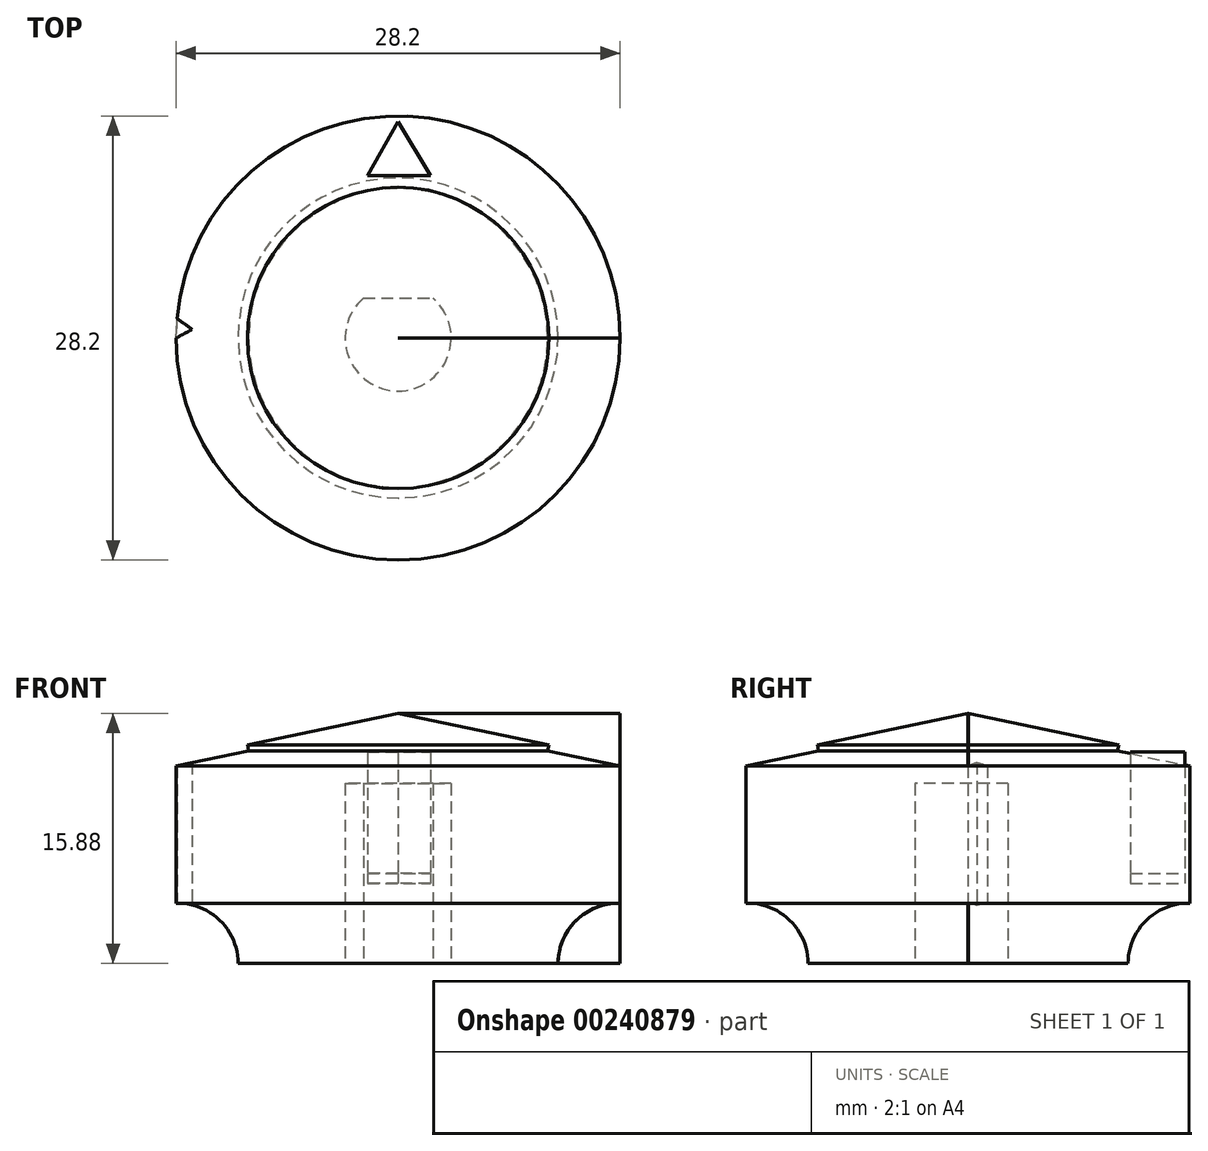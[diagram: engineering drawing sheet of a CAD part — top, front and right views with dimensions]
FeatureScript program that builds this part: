
annotation { "Feature Type Name" : "Feature", "Feature Type Description" : "" }
export const myFeature = defineFeature(function(context is Context, id is Id, definition is map)
    precondition{}
    {
        {
            var Q0;
            Q0=qCreatedBy(makeId("Top.planeOp"),FACE);
            cPlane(context, id + "F0", {"entities" : qUnion([Q0]), "cplaneType" : CPlaneType.OFFSET, "offset" : 5.08 * mm, "width" : 152.4 * mm, "height" : 152.4 * mm});
        }
        {
            var Q0;
            Q0=qCreatedBy(makeId("Top.planeOp"),FACE);
            var sketch = newSketch(context, id + "F1", { "sketchPlane" : qUnion([Q0])});
            skCircle(sketch, "E0", {"center": v(0, 0) * mm, "radius": 14.1 * mm});
            skSolve(sketch);
        }
        {
            var Q0;
            Q0 = qSketchRegion(id + "F1", true);
            extrude(context, id + "F2", {"entities" : qUnion([Q0]), "depth" : 15.88 * mm});
        }
        {
            var Q0;
            Q0=qCreatedBy(makeId("Front.planeOp"),FACE);
            var sketch = newSketch(context, id + "F3", { "sketchPlane" : qUnion([Q0])});
            skLineSegment(sketch, "E1", {"start": v(0, 0) * mm, "end": v(0, 31.75) * mm, "construction": true});
            skLineSegment(sketch, "E2", {"start": v(0, 15.88) * mm, "end": v(9.57, 13.87) * mm});
            skLineSegment(sketch, "E3", {"start": v(0, 15.88) * mm, "end": v(14.58, 15.88) * mm});
            skLineSegment(sketch, "E4", {"start": v(14.58, 12.83) * mm, "end": v(14.58, 15.88) * mm});
            skLineSegment(sketch, "E5", {"start": v(9.57, 13.87) * mm, "end": v(9.5, 13.5) * mm});
            skLineSegment(sketch, "E6", {"start": v(9.5, 13.5) * mm, "end": v(14.49, 12.46) * mm});
            skLineSegment(sketch, "E7", {"start": v(14.49, 12.46) * mm, "end": v(14.58, 12.83) * mm});
            skLineSegment(sketch, "E8", {"start": v(0, 0) * mm, "end": v(10.16, 0) * mm, "construction": true});
            skArc(sketch, "E9", {"start": v(14.1, 3.82) * mm, "mid": v(11.32, 2.74) * mm, "end": v(10.16, 0) * mm});
            skLineSegment(sketch, "E10", {"start": v(14.1, 3.82) * mm, "end": v(14.1, 0) * mm});
            skLineSegment(sketch, "E11", {"start": v(10.16, 0) * mm, "end": v(14.1, 0) * mm});
            skSolve(sketch);
        }
        {
            var Q0;
            Q0 = qSketchRegion(id + "F3", true);
            var Q1;
            Q1=sQuery(id+"F3.wireOp",EDGE,"E1");
            revolve(context, id + "F4", {"operationType" : NewBodyOperationType.REMOVE, "entities" : qUnion([Q0]), "axis" : qUnion([Q1]), "revolveType" : RevolveType.ONE_DIRECTION, "oppositeDirection" : true, "angle" : 359.9 * degree});
        }
        {
            var Q0;
            Q0=qCreatedBy(id+"F0.planeOp",FACE);
            var sketch = newSketch(context, id + "F5", { "sketchPlane" : qUnion([Q0])});
            skLineSegment(sketch, "E12", {"start": v(0, 13.76) * mm, "end": v(-1.95, 10.3) * mm});
            skLineSegment(sketch, "E13", {"start": v(-1.95, 10.3) * mm, "end": v(2.04, 10.3) * mm});
            skLineSegment(sketch, "E14", {"start": v(2.04, 10.3) * mm, "end": v(0, 13.76) * mm});
            skSolve(sketch);
        }
        {
            var Q0;
            Q0 = qSketchRegion(id + "F5", true);
            extrude(context, id + "F6", {"entities" : qUnion([Q0]), "depth" : 0.63 * mm});
        }
        {
            var Q0;
            Q0 = qSketchRegion(id + "F5", true);
            extrude(context, id + "F7", {"entities" : qUnion([Q0]), "depth" : 8.36 * mm});
        }
        {
            var Q0;
            Q0=makeQuery(id+"F2.opExtrude","CAP_FACE",FACE,{"disambiguationData":[OSD([sQuery(id+"F1.wireOp",EDGE,"E0")])],"isStart":true});
            var sketch = newSketch(context, id + "F8", { "sketchPlane" : qUnion([Q0])});
            skArc(sketch, "E15", {"start": v(2.2, -2.54) * mm, "mid": v(0, 3.37) * mm, "end": v(-2.2, -2.54) * mm});
            skLineSegment(sketch, "E16", {"start": v(-2.2, -2.54) * mm, "end": v(2.2, -2.54) * mm});
            skSolve(sketch);
        }
        {
            var Q0;
            Q0 = qSketchRegion(id + "F8", true);
            extrude(context, id + "F9", {"entities" : qUnion([Q0]), "operationType" : NewBodyOperationType.REMOVE, "oppositeDirection" : true, "depth" : 11.43 * mm});
        }
        {
            var Q0;
            Q0=qCreatedBy(makeId("Top.planeOp"),FACE);
            var sketch = newSketch(context, id + "F10", { "sketchPlane" : qUnion([Q0])});
            skLineSegment(sketch, "E17", {"start": v(0, 0) * mm, "end": v(-14.1, 0) * mm, "construction": true});
            skLineSegment(sketch, "E18", {"start": v(0, 0) * mm, "end": v(-14.04, 1.23) * mm, "construction": true});
            skLineSegment(sketch, "E19", {"start": v(-14.1, 0) * mm, "end": v(-13.07, 0.55) * mm});
            skLineSegment(sketch, "E20", {"start": v(-13.07, 0.55) * mm, "end": v(-14.04, 1.23) * mm});
            skLineSegment(sketch, "E21", {"start": v(-14.04, 1.23) * mm, "end": v(-14.1, 0) * mm});
            skSolve(sketch);
        }
        {
            var Q0;
            Q0 = qSketchRegion(id + "F10", true);
            extrude(context, id + "F11", {"entities" : qUnion([Q0]), "operationType" : NewBodyOperationType.REMOVE, "endBound" : BoundingType.THROUGH_ALL, "depth" : 25.4 * mm});
        }
    });
